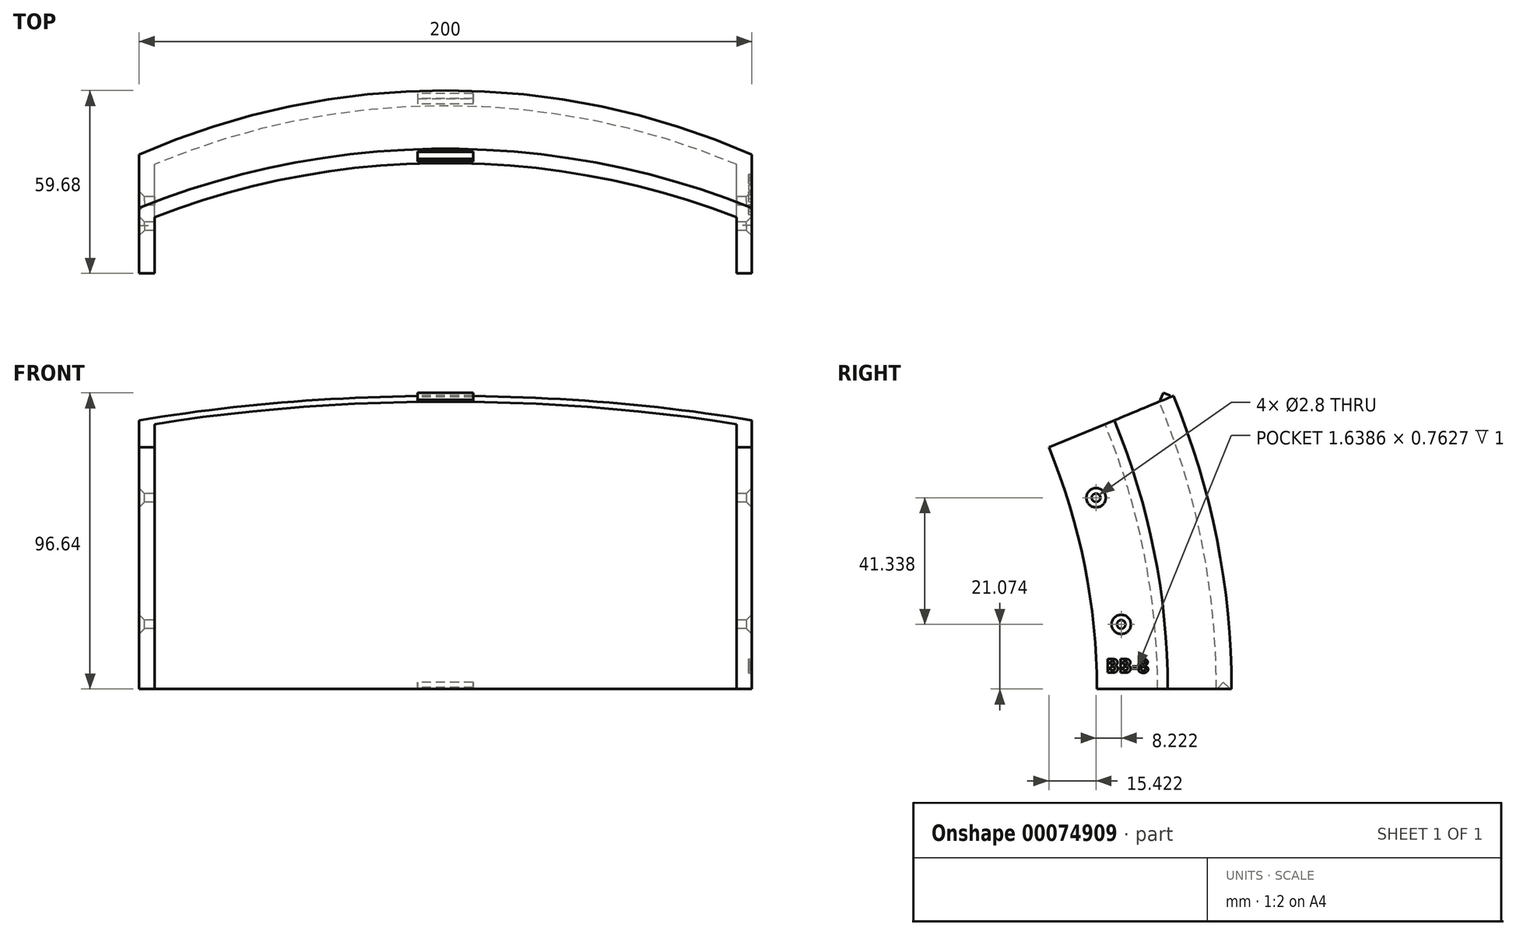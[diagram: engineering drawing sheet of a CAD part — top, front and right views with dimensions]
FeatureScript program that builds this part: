
annotation { "Feature Type Name" : "Feature", "Feature Type Description" : "" }
export const myFeature = defineFeature(function(context is Context, id is Id, definition is map)
    precondition{}
    {
        {
            var Q0;
            Q0=qCreatedBy(makeId("Top.planeOp"),FACE);
            var sketch = newSketch(context, id + "F0", { "sketchPlane" : qUnion([Q0])});
            skArc(sketch, "E0", {"start": v(-95, 225.83) * mm, "mid": v(0, 245) * mm, "end": v(95, 225.83) * mm});
            skArc(sketch, "E1", {"start": v(-100, 229.13) * mm, "mid": v(0, 250) * mm, "end": v(100, 229.13) * mm});
            skLineSegment(sketch, "E2", {"start": v(-100, 229.13) * mm, "end": v(-100, 206) * mm});
            skLineSegment(sketch, "E3", {"start": v(-100, 206) * mm, "end": v(-95, 206) * mm});
            skLineSegment(sketch, "E4", {"start": v(100, 229.13) * mm, "end": v(100, 206) * mm});
            skLineSegment(sketch, "E5", {"start": v(100, 206) * mm, "end": v(95, 206) * mm});
            skLineSegment(sketch, "E6", {"start": v(-95, 0) * mm, "end": v(95, 0) * mm, "construction": true});
            skLineSegment(sketch, "E7", {"start": v(-95, 206) * mm, "end": v(-95, 0) * mm, "construction": true});
            skLineSegment(sketch, "E8", {"start": v(95, 206) * mm, "end": v(95, 225.83) * mm});
            skLineSegment(sketch, "E9", {"start": v(-95, 206) * mm, "end": v(-95, 225.83) * mm});
            skLineSegment(sketch, "E10", {"start": v(95, 0) * mm, "end": v(95, 206) * mm, "construction": true});
            skPoint(sketch, "E11.positionSnap0", {"position": v(0, 225) * mm});
            skLineSegment(sketch, "E12", {"start": v(-95, 225.83) * mm, "end": v(95, 225.83) * mm, "construction": true});
            skPoint(sketch, "E13", {"position": v(0, 225.83) * mm});
            skLineSegment(sketch, "E14", {"start": v(95, 225.83) * mm, "end": v(89.8, 225.83) * mm});
            skLineSegment(sketch, "E15", {"start": v(-95, 225.83) * mm, "end": v(-89.8, 225.83) * mm});
            skLineSegment(sketch, "E16", {"start": v(-89.8, 225.83) * mm, "end": v(-89.8, 220.83) * mm});
            skLineSegment(sketch, "E17", {"start": v(-89.8, 220.83) * mm, "end": v(-85, 220.83) * mm});
            skLineSegment(sketch, "E18", {"start": v(-85, 220.83) * mm, "end": v(-85, 229.78) * mm});
            skLineSegment(sketch, "E19", {"start": v(89.8, 225.83) * mm, "end": v(89.8, 220.83) * mm});
            skLineSegment(sketch, "E20", {"start": v(89.8, 220.83) * mm, "end": v(85, 220.83) * mm});
            skLineSegment(sketch, "E21", {"start": v(85, 220.83) * mm, "end": v(85, 229.78) * mm});
            skLineSegment(sketch, "E22.bottom", {"start": v(9.04, 249.04) * mm, "end": v(-9.04, 249.04) * mm});
            skLineSegment(sketch, "E22.top", {"start": v(9.04, 245.63) * mm, "end": v(-9.04, 245.63) * mm});
            skLineSegment(sketch, "E22.left", {"start": v(9.04, 249.04) * mm, "end": v(9.04, 245.63) * mm});
            skLineSegment(sketch, "E22.right", {"start": v(-9.04, 249.04) * mm, "end": v(-9.04, 245.63) * mm});
            skPoint(sketch, "E22.middle", {"position": v(0, 247.34) * mm});
            skLineSegment(sketch, "E23.bottom", {"start": v(95, 225.83) * mm, "end": v(94, 225.83) * mm});
            skLineSegment(sketch, "E23.top", {"start": v(95, 206) * mm, "end": v(94, 206) * mm});
            skLineSegment(sketch, "E23.left", {"start": v(95, 225.83) * mm, "end": v(95, 206) * mm});
            skLineSegment(sketch, "E23.right", {"start": v(94, 225.83) * mm, "end": v(94, 206) * mm});
            skLineSegment(sketch, "E24.bottom", {"start": v(-95, 225.83) * mm, "end": v(-94, 225.83) * mm});
            skLineSegment(sketch, "E24.top", {"start": v(-95, 206) * mm, "end": v(-94, 206) * mm});
            skLineSegment(sketch, "E24.left", {"start": v(-95, 225.83) * mm, "end": v(-95, 206) * mm});
            skLineSegment(sketch, "E24.right", {"start": v(-94, 225.83) * mm, "end": v(-94, 206) * mm});
            skSolve(sketch);
        }
        {
            var Q0;
            Q0=makeQuery(id+"F0.imprint","IMPRINT",FACE,{"disambiguationData":[TD([[makeQuery(id+"F0.imprint","IMPRINT",EDGE,{"derivedFrom":sQuery(id+"F0.wireOp",EDGE,"E1")}),-1.0]])]});
            var Q1;
            {var subQ0=sQuery(id+"F0.wireOp",EDGE,"lmNdPizv-3n6S-nKX4-SDGa-ncaC4Ag9tuAc");var subQ1=sQuery(id+"F0.wireOp",EDGE,"E0");var subQ2=makeQuery(id+"F0.imprint","INTERSECT",VERTEX,{"disambiguationData":[OD(0.0)],"derivedFrom":[subQ1,subQ0]});Q1=makeQuery(id+"F0.imprint","IMPRINT",FACE,{"disambiguationData":[TD([[makeQuery(id+"F0.imprint","IMPRINT",EDGE,{"disambiguationData":[TD([[subQ2,-1.0]])],"derivedFrom":subQ1}),-1.0]])]});}
            var Q2;
            {var subQ0=sQuery(id+"F0.wireOp",EDGE,"lmNdPizv-3n6S-nKX4-SDGa-ncaC4Ag9tuAc");var subQ1=sQuery(id+"F0.wireOp",EDGE,"E0");var subQ2=makeQuery(id+"F0.imprint","INTERSECT",VERTEX,{"disambiguationData":[OD(1.0)],"derivedFrom":[subQ1,subQ0]});Q2=makeQuery(id+"F0.imprint","IMPRINT",FACE,{"disambiguationData":[TD([[makeQuery(id+"F0.imprint","IMPRINT",EDGE,{"disambiguationData":[TD([[subQ2,1.0]])],"derivedFrom":subQ1}),-1.0]])]});}
            var Q3;
            {var subQ4=sQuery(id+"F0.wireOp",EDGE,"bwZ3USKc-1TmK-ejq0-4772-UZMCS9pa2qVR");Q3=makeQuery(id+"F0.imprint","IMPRINT",FACE,{"disambiguationData":[TD([[makeQuery(id+"F0.imprint","IMPRINT",EDGE,{"derivedFrom":subQ4}),1.0]])]});}
            var Q4;
            {var subQ4=sQuery(id+"F0.wireOp",EDGE,"LWuvFovu-X8zo-2N0G-cAHU-RIiqH0PJfQXl");Q4=makeQuery(id+"F0.imprint","IMPRINT",FACE,{"disambiguationData":[TD([[makeQuery(id+"F0.imprint","IMPRINT",EDGE,{"derivedFrom":subQ4}),-1.0]])]});}
            var Q5;
            {var subQ0=sQuery(id+"F0.wireOp",EDGE,"pbFOqv5W-1PVb-HM3S-Wum6-j1YJo5w8kIsj");Q5=makeQuery(id+"F0.imprint","IMPRINT",FACE,{"disambiguationData":[TD([[makeQuery(id+"F0.imprint","IMPRINT",EDGE,{"derivedFrom":subQ0}),-1.0]])]});}
            var Q6;
            {var subQ0=sQuery(id+"F0.wireOp",EDGE,"D48Q59Sa-7qnU-lKWU-Bux8-1BkC7HTLLyOH");Q6=makeQuery(id+"F0.imprint","IMPRINT",FACE,{"disambiguationData":[TD([[makeQuery(id+"F0.imprint","IMPRINT",EDGE,{"derivedFrom":subQ0}),1.0]])]});}
            var Q7;
            Q7=makeQuery(id+"F0.imprint","IMPRINT",FACE,{"disambiguationData":[TD([[makeQuery(id+"F0.imprint","IMPRINT",EDGE,{"derivedFrom":sQuery(id+"F0.wireOp",EDGE,"E22.bottom")}),1.0]])]});
            var Q8;
            Q8=sQuery(id+"F0.wireOp",EDGE,"E6");
            revolve(context, id + "F1", {"entities" : qUnion([Q0, Q1, Q2, Q3, Q4, Q5, Q6, Q7]), "axis" : qUnion([Q8]), "revolveType" : RevolveType.ONE_DIRECTION, "angle" : 22.5 * degree});
        }
        {
            var Q0;
            Q0=qCreatedBy(makeId("Right.planeOp"),FACE);
            var sketch = newSketch(context, id + "F2", { "sketchPlane" : qUnion([Q0])});
            skLineSegment(sketch, "E25", {"start": v(0, 0) * mm, "end": v(205.74, 62.41) * mm, "construction": true});
            skCircle(sketch, "E26", {"center": v(205.74, 62.41) * mm, "radius": 1.4 * mm});
            skCircle(sketch, "E27.1.0", {"center": v(213.96, 21.07) * mm, "radius": 1.4 * mm});
            skPoint(sketch, "E27.center", {"position": v(0, 0) * mm});
            skLineSegment(sketch, "E27.anchor2", {"start": v(0, 0) * mm, "end": v(213.96, 21.07) * mm, "construction": true});
            skSolve(sketch);
        }
        {
            var Q0;
            Q0=makeQuery(id+"F1.opRevolve","SWEPT_FACE",FACE,{"disambiguationData":[OSD([sQuery(id+"F0.wireOp",EDGE,"E4")])]});
            var sketch = newSketch(context, id + "F3", { "sketchPlane" : qUnion([Q0])});
            skText(sketch, "E28", { "text": "BB-8", "fontName": "OpenSans-Bold.ttf"});
            const initialGuessF3  = {"E28": [0.20896, 0.00532, 1, 0, 0.0045]};
            skSetInitialGuess(sketch, initialGuessF3);
            skSolve(sketch);
        }
        {
            var Q0;
            Q0 = qSketchRegion(id + "F3", true);
            extrude(context, id + "F4", {"entities" : qUnion([Q0]), "operationType" : NewBodyOperationType.REMOVE, "oppositeDirection" : true, "depth" : 1 * mm});
        }
        {
            var Q0;
            Q0=makeQuery(id+"F0.imprint","IMPRINT",FACE,{"disambiguationData":[TD([[makeQuery(id+"F0.imprint","IMPRINT",EDGE,{"derivedFrom":sQuery(id+"F0.wireOp",EDGE,"E22.bottom")}),1.0]])]});
            var Q1;
            Q1=sQuery(id+"F0.wireOp",EDGE,"E6");
            revolve(context, id + "F5", {"operationType" : NewBodyOperationType.ADD, "entities" : qUnion([Q0]), "axis" : qUnion([Q1]), "revolveType" : RevolveType.ONE_DIRECTION, "angle" : 23 * degree});
        }
        {
            var Q0;
            Q0=makeQuery(id+"F0.imprint","IMPRINT",FACE,{"disambiguationData":[TD([[makeQuery(id+"F0.imprint","IMPRINT",EDGE,{"derivedFrom":sQuery(id+"F0.wireOp",EDGE,"E22.bottom")}),1.0]])]});
            var Q1;
            Q1=sQuery(id+"F0.wireOp",EDGE,"E6");
            revolve(context, id + "F6", {"entities" : qUnion([Q0]), "axis" : qUnion([Q1]), "revolveType" : RevolveType.ONE_DIRECTION, "angle" : .5 * degree});
        }
        {
            var Q0;
            Q0=makeQuery(id+"F2.imprint","IMPRINT",FACE,{"disambiguationData":[TD([[makeQuery(id+"F2.imprint","IMPRINT",EDGE,{"derivedFrom":sQuery(id+"F2.wireOp",EDGE,"E26")}),1.0]])]});
            var Q1;
            Q1=makeQuery(id+"F2.imprint","IMPRINT",FACE,{"disambiguationData":[TD([[makeQuery(id+"F2.imprint","IMPRINT",EDGE,{"derivedFrom":sQuery(id+"F2.wireOp",EDGE,"E27.1.0")}),1.0]])]});
            extrude(context, id + "F7", {"entities" : qUnion([Q0, Q1]), "operationType" : NewBodyOperationType.REMOVE, "depth" : 278.72 * mm, "symmetric" : true});
        }
        {
            var Q0;
            Q0=makeQuery(id+"F7.boolean.opBoolean","INTERSECT",EDGE,{"derivedFrom":[makeQuery(id+"F1.opRevolve","SWEPT_FACE",FACE,{"disambiguationData":[OSD([sQuery(id+"F0.wireOp",EDGE,"E4")])]}),makeQuery(id+"F7.opExtrude","SWEPT_FACE",FACE,{"disambiguationData":[OSD([sQuery(id+"F2.wireOp",EDGE,"E27.1.0")])]})]});
            var Q1;
            Q1=makeQuery(id+"F7.boolean.opBoolean","INTERSECT",EDGE,{"derivedFrom":[makeQuery(id+"F1.opRevolve","SWEPT_FACE",FACE,{"disambiguationData":[OSD([sQuery(id+"F0.wireOp",EDGE,"E4")])]}),makeQuery(id+"F7.opExtrude","SWEPT_FACE",FACE,{"disambiguationData":[OSD([sQuery(id+"F2.wireOp",EDGE,"E26")])]})]});
            var Q2;
            Q2=makeQuery(id+"F7.boolean.opBoolean","INTERSECT",EDGE,{"derivedFrom":[makeQuery(id+"F1.opRevolve","SWEPT_FACE",FACE,{"disambiguationData":[OSD([sQuery(id+"F0.wireOp",EDGE,"E2")])]}),makeQuery(id+"F7.opExtrude","SWEPT_FACE",FACE,{"disambiguationData":[OSD([sQuery(id+"F2.wireOp",EDGE,"E27.1.0")])]})]});
            var Q3;
            Q3=makeQuery(id+"F7.boolean.opBoolean","INTERSECT",EDGE,{"derivedFrom":[makeQuery(id+"F1.opRevolve","SWEPT_FACE",FACE,{"disambiguationData":[OSD([sQuery(id+"F0.wireOp",EDGE,"E2")])]}),makeQuery(id+"F7.opExtrude","SWEPT_FACE",FACE,{"disambiguationData":[OSD([sQuery(id+"F2.wireOp",EDGE,"E26")])]})]});
            chamfer(context, id + "F8", {"entities" : qUnion([Q0, Q1, Q2, Q3]), "width" : 1.75 * mm, "tangentPropagation" : true});
        }
        {
            var Q0;
            Q0=makeQuery(id+"F5.opRevolve","CAP_EDGE",EDGE,{"disambiguationData":[OSD([sQuery(id+"F0.wireOp",EDGE,"E22.bottom")])],"isStart":false});
            var Q1;
            Q1=makeQuery(id+"F5.opRevolve","CAP_EDGE",EDGE,{"disambiguationData":[OSD([sQuery(id+"F0.wireOp",EDGE,"E22.top")])],"isStart":false});
            chamfer(context, id + "F9", {"entities" : qUnion([Q0, Q1]), "width" : 1.7 * mm, "tangentPropagation" : true});
        }
        {
            var Q0;
            Q0=makeQuery(id+"F6.opRevolve","CAP_EDGE",EDGE,{"disambiguationData":[OSD([sQuery(id+"F0.wireOp",EDGE,"E22.bottom")])],"isStart":false});
            var Q1;
            Q1=makeQuery(id+"F6.opRevolve","CAP_EDGE",EDGE,{"disambiguationData":[OSD([sQuery(id+"F0.wireOp",EDGE,"E22.top")])],"isStart":false});
            chamfer(context, id + "F10", {"entities" : qUnion([Q0, Q1]), "width" : 1.7 * mm, "tangentPropagation" : true});
        }
        {
            var Q0;
            Q0=makeQuery(id+"F6.opRevolve","SWEPT_BODY",BODY,{"disambiguationData":[OSD([sQuery(id+"F0.wireOp",EDGE,"E22.bottom"),sQuery(id+"F0.wireOp",EDGE,"E22.top"),sQuery(id+"F0.wireOp",EDGE,"E22.left"),sQuery(id+"F0.wireOp",EDGE,"E22.right")])]});
            var Q1;
            Q1=makeQuery(id+"F1.opRevolve","SWEPT_BODY",BODY,{"disambiguationData":[OSD([sQuery(id+"F0.wireOp",EDGE,"E0"),sQuery(id+"F0.wireOp",EDGE,"E1"),sQuery(id+"F0.wireOp",EDGE,"E2"),sQuery(id+"F0.wireOp",EDGE,"E3"),sQuery(id+"F0.wireOp",EDGE,"E4"),sQuery(id+"F0.wireOp",EDGE,"E5"),sQuery(id+"F0.wireOp",EDGE,"E14"),sQuery(id+"F0.wireOp",EDGE,"E15"),sQuery(id+"F0.wireOp",EDGE,"E16"),sQuery(id+"F0.wireOp",EDGE,"E17"),sQuery(id+"F0.wireOp",EDGE,"E18"),sQuery(id+"F0.wireOp",EDGE,"E19"),sQuery(id+"F0.wireOp",EDGE,"E20"),sQuery(id+"F0.wireOp",EDGE,"E21"),sQuery(id+"F0.wireOp",EDGE,"E23.bottom"),sQuery(id+"F0.wireOp",EDGE,"E23.left"),sQuery(id+"F0.wireOp",EDGE,"E24.bottom"),sQuery(id+"F0.wireOp",EDGE,"E24.left")])]});
            booleanBodies(context, id + "F11", {"operationType" : BooleanOperationType.SUBTRACTION, "tools" : qUnion([Q0]), "targets" : qUnion([Q1])});
        }
    });
